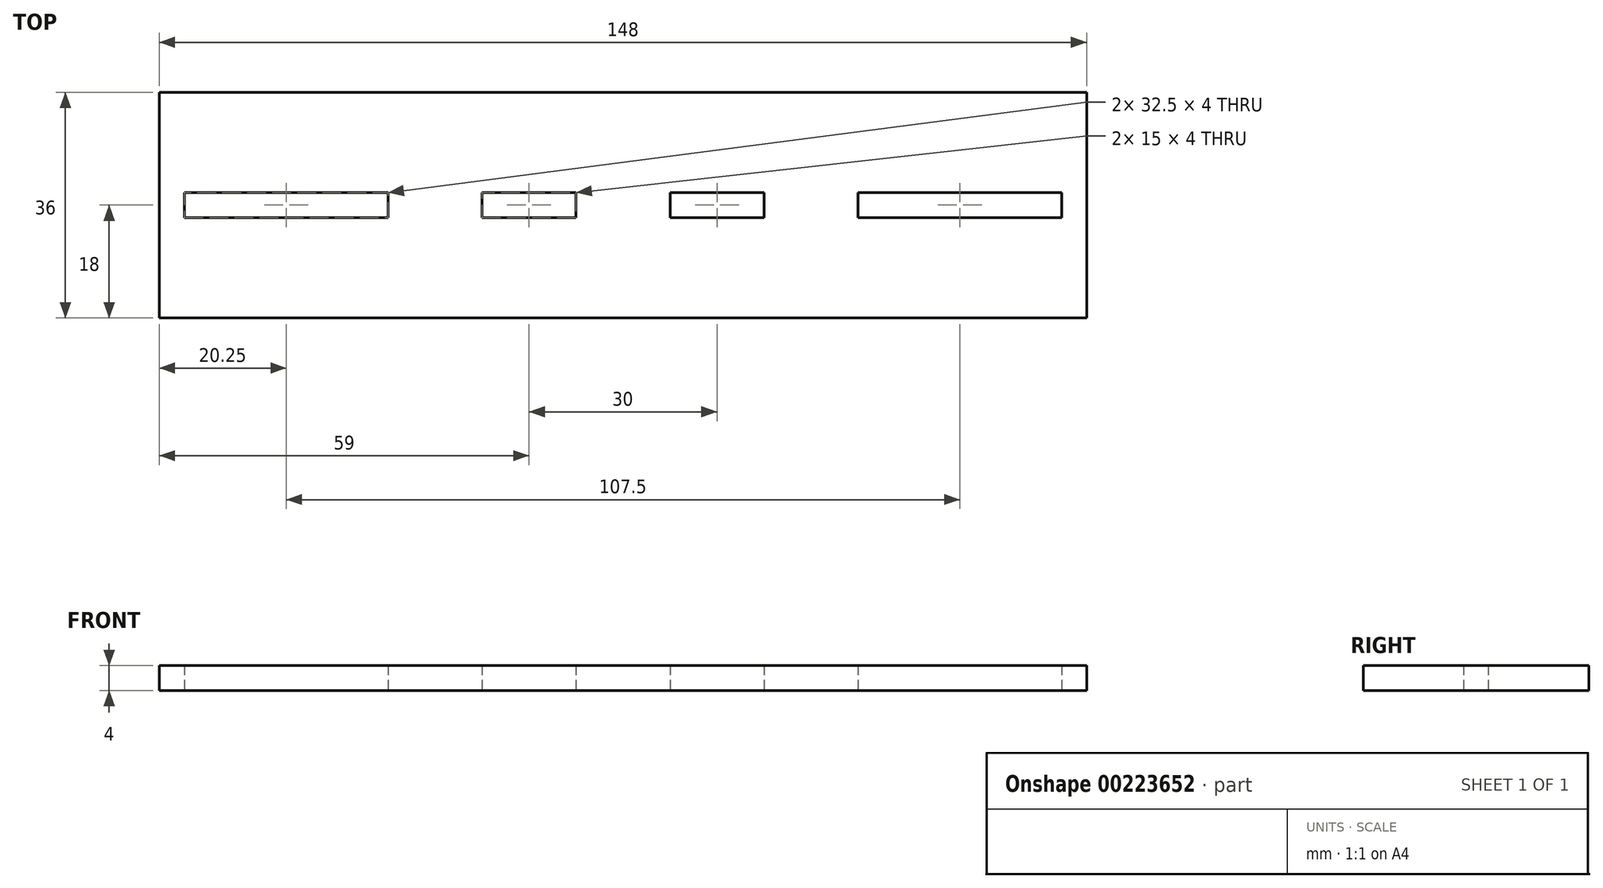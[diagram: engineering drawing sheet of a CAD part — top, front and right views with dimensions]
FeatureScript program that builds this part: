
annotation { "Feature Type Name" : "Feature", "Feature Type Description" : "" }
export const myFeature = defineFeature(function(context is Context, id is Id, definition is map)
    precondition{}
    {
        {
            var Q0;
            Q0=qCreatedBy(makeId("Top.planeOp"),FACE);
            var sketch = newSketch(context, id + "F0", { "sketchPlane" : qUnion([Q0])});
            skLineSegment(sketch, "E0", {"start": v(0, 0) * mm, "end": v(-148, 0) * mm});
            skLineSegment(sketch, "E1", {"start": v(-148, -36) * mm, "end": v(0, -36) * mm});
            skLineSegment(sketch, "E2", {"start": v(-148, 0) * mm, "end": v(-148, -16) * mm});
            skLineSegment(sketch, "E3", {"start": v(-148, -16) * mm, "end": v(-148, -20) * mm});
            skLineSegment(sketch, "E4", {"start": v(-148, -20) * mm, "end": v(-148, -36) * mm});
            skLineSegment(sketch, "E5", {"start": v(0, 0) * mm, "end": v(0, -16) * mm});
            skLineSegment(sketch, "E6", {"start": v(0, -16) * mm, "end": v(0, -20) * mm});
            skLineSegment(sketch, "E7", {"start": v(0, -20) * mm, "end": v(0, -36) * mm});
            skLineSegment(sketch, "E8", {"start": v(-111.5, -16) * mm, "end": v(-111.5, -16) * mm});
            skLineSegment(sketch, "E9", {"start": v(-96.5, -16) * mm, "end": v(-81.5, -16) * mm});
            skLineSegment(sketch, "E10", {"start": v(-36.5, -16) * mm, "end": v(-4, -16) * mm});
            skLineSegment(sketch, "E11", {"start": v(-144, -16) * mm, "end": v(-144, -20) * mm});
            skLineSegment(sketch, "E12", {"start": v(-111.5, -16) * mm, "end": v(-111.5, -20) * mm});
            skLineSegment(sketch, "E13", {"start": v(-96.5, -16) * mm, "end": v(-96.5, -20) * mm});
            skLineSegment(sketch, "E14", {"start": v(-81.5, -16) * mm, "end": v(-81.5, -20) * mm});
            skLineSegment(sketch, "E15", {"start": v(-66.5, -16) * mm, "end": v(-66.5, -20) * mm});
            skLineSegment(sketch, "E16", {"start": v(-51.5, -16) * mm, "end": v(-51.5, -20) * mm});
            skLineSegment(sketch, "E17", {"start": v(-36.5, -16) * mm, "end": v(-36.5, -20) * mm});
            skLineSegment(sketch, "E18", {"start": v(-4, -16) * mm, "end": v(-4, -20) * mm});
            skLineSegment(sketch, "E19", {"start": v(-144, -16) * mm, "end": v(-111.5, -16) * mm});
            skLineSegment(sketch, "E20", {"start": v(-144, -20) * mm, "end": v(-111.5, -20) * mm});
            skLineSegment(sketch, "E21", {"start": v(-96.5, -20) * mm, "end": v(-81.5, -20) * mm});
            skLineSegment(sketch, "E22", {"start": v(-51.5, -20) * mm, "end": v(-66.5, -20) * mm});
            skLineSegment(sketch, "E23", {"start": v(-66.5, -16) * mm, "end": v(-51.5, -16) * mm});
            skLineSegment(sketch, "E24", {"start": v(-36.5, -20) * mm, "end": v(-4, -20) * mm});
            skSolve(sketch);
        }
        {
            var Q0;
            Q0=makeQuery(id+"F0.imprint","IMPRINT",FACE,{"disambiguationData":[TD([[makeQuery(id+"F0.imprint","IMPRINT",EDGE,{"derivedFrom":sQuery(id+"F0.wireOp",EDGE,"E0")}),1.0]])]});
            extrude(context, id + "F1", {"entities" : qUnion([Q0]), "depth" : 4 * mm});
        }
    });
